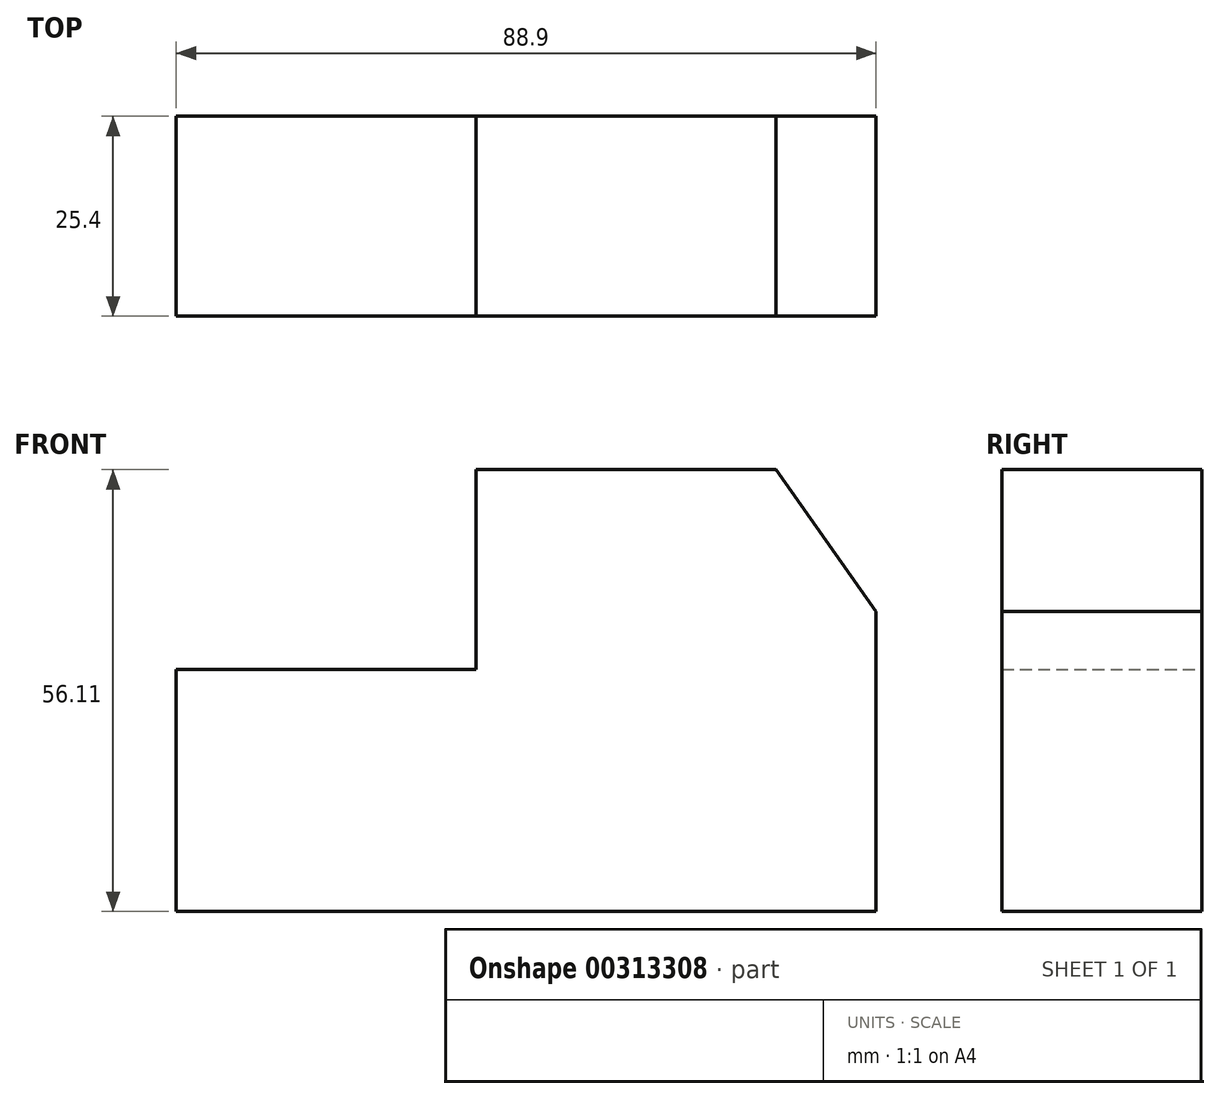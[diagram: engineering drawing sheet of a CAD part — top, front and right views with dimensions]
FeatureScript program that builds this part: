
annotation { "Feature Type Name" : "Feature", "Feature Type Description" : "" }
export const myFeature = defineFeature(function(context is Context, id is Id, definition is map)
    precondition{}
    {
        {
            var Q0;
            Q0=qCreatedBy(makeId("Front.planeOp"),FACE);
            var sketch = newSketch(context, id + "F0", { "sketchPlane" : qUnion([Q0])});
            skLineSegment(sketch, "E0", {"start": v(-48.58, -38.1) * mm, "end": v(40.32, -38.1) * mm});
            skLineSegment(sketch, "E1", {"start": v(40.32, -38.1) * mm, "end": v(40.32, 0) * mm});
            skLineSegment(sketch, "E2", {"start": v(40.32, 0) * mm, "end": v(27.62, 18.01) * mm});
            skLineSegment(sketch, "E3", {"start": v(27.62, 18.01) * mm, "end": v(-10.48, 18.01) * mm});
            skLineSegment(sketch, "E4", {"start": v(-10.48, 18.01) * mm, "end": v(-10.48, -7.39) * mm});
            skLineSegment(sketch, "E5", {"start": v(-10.48, -7.39) * mm, "end": v(-48.58, -7.39) * mm});
            skLineSegment(sketch, "E6", {"start": v(-48.58, -7.39) * mm, "end": v(-48.58, -38.1) * mm});
            skSolve(sketch);
        }
        {
            var Q0;
            Q0=makeQuery(id+"F0.imprint","IMPRINT",FACE,{"disambiguationData":[TD([[makeQuery(id+"F0.imprint","IMPRINT",EDGE,{"derivedFrom":sQuery(id+"F0.wireOp",EDGE,"E0")}),1.0]])]});
            extrude(context, id + "F1", {"entities" : qUnion([Q0]), "depth" : 25.4 * mm});
        }
    });
